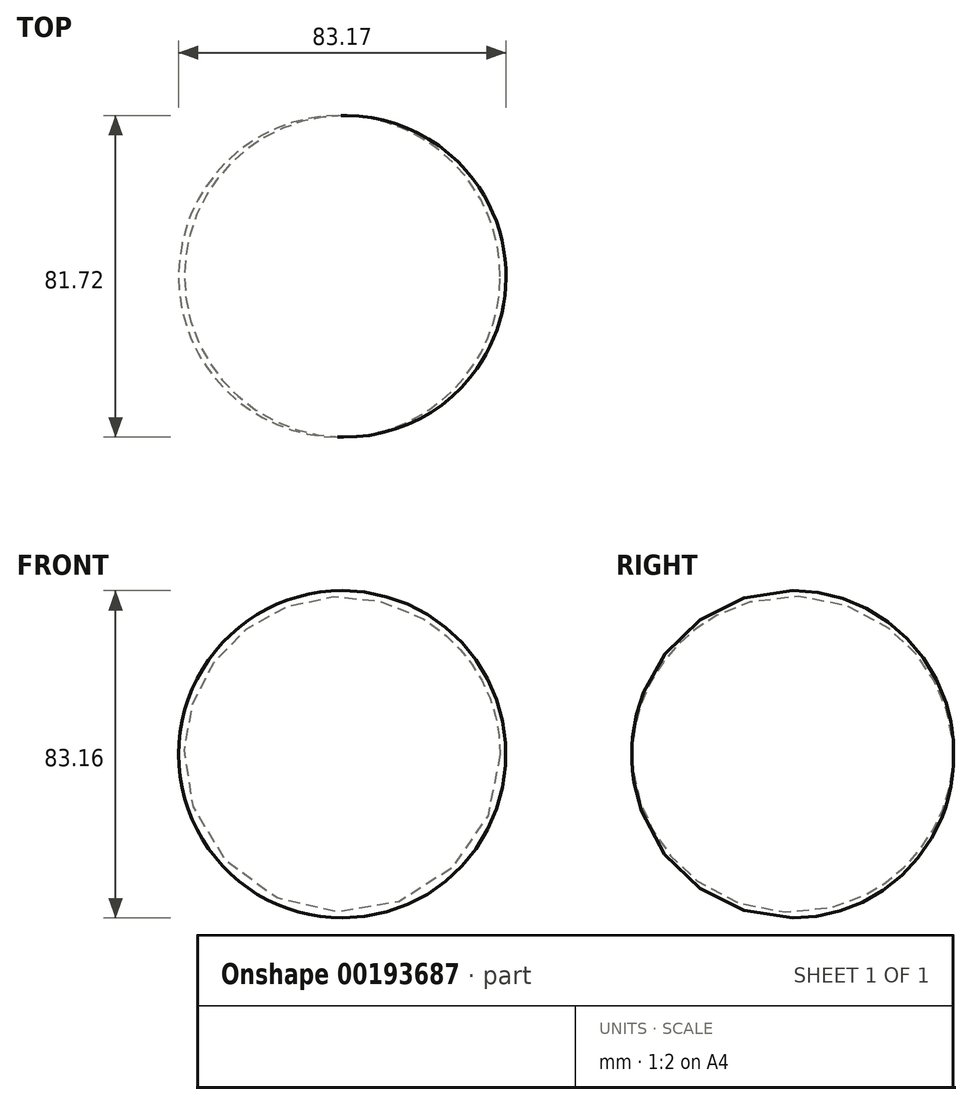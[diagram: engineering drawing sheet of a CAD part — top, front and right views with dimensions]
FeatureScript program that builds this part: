
annotation { "Feature Type Name" : "Feature", "Feature Type Description" : "" }
export const myFeature = defineFeature(function(context is Context, id is Id, definition is map)
    precondition{}
    {
        {
            var Q0;
            Q0=qCreatedBy(makeId("Top.planeOp"),FACE);
            var sketch = newSketch(context, id + "F0", { "sketchPlane" : qUnion([Q0])});
            skArc(sketch, "E0", {"start": v(1.19, 40.83) * mm, "mid": v(-40.85, 0.45) * mm, "end": v(0.28, -40.85) * mm});
            skLineSegment(sketch, "E1", {"start": v(40.83, -1.26) * mm, "end": v(40.83, -1.26) * mm});
            skLineSegment(sketch, "E2", {"start": v(1.19, 40.83) * mm, "end": v(0.28, -40.85) * mm});
            skSolve(sketch);
        }
        {
            var Q0;
            Q0 = qSketchRegion(id + "F0", true);
            var Q1;
            Q1=sQuery(id+"F0.wireOp",EDGE,"E2");
            revolve(context, id + "F1", {"entities" : qUnion([Q0]), "axis" : qUnion([Q1]), "revolveType" : RevolveType.FULL});
        }
    });
